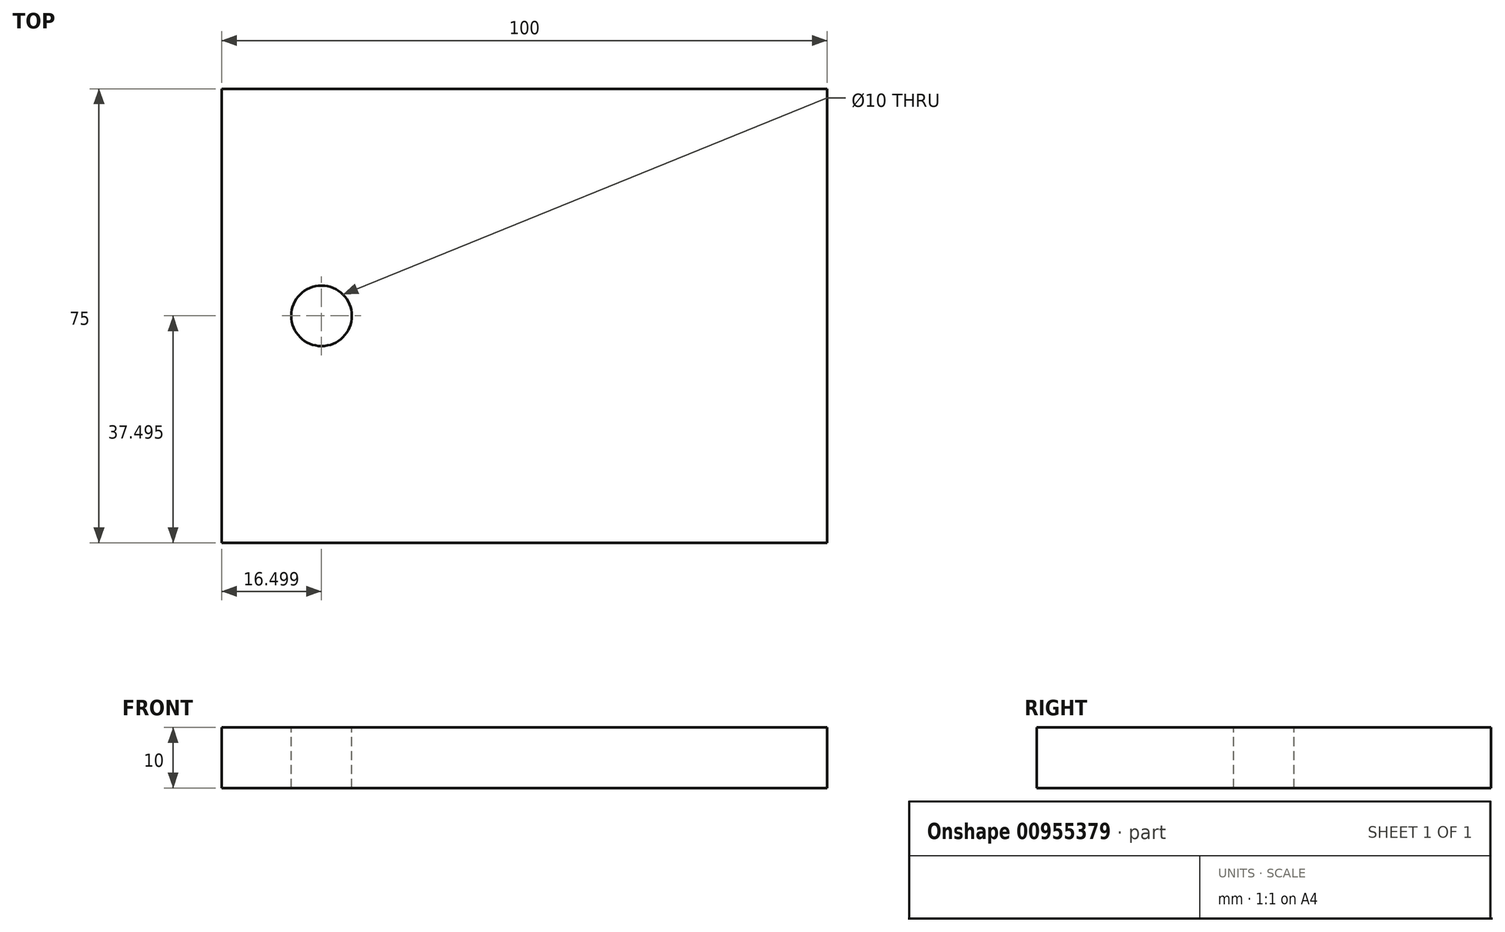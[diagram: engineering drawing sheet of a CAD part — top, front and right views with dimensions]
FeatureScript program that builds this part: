
annotation { "Feature Type Name" : "Feature", "Feature Type Description" : "" }
export const myFeature = defineFeature(function(context is Context, id is Id, definition is map)
    precondition{}
    {
        {
            var Q0;
            Q0=qCreatedBy(makeId("Top.planeOp"),FACE);
            var sketch = newSketch(context, id + "F0", { "sketchPlane" : qUnion([Q0])});
            skLineSegment(sketch, "E0.bottom", {"start": v(51.9, 49.62) * mm, "end": v(-48.1, 49.62) * mm});
            skLineSegment(sketch, "E0.top", {"start": v(51.9, -25.38) * mm, "end": v(-48.1, -25.38) * mm});
            skLineSegment(sketch, "E0.left", {"start": v(51.9, 49.62) * mm, "end": v(51.9, -25.38) * mm});
            skLineSegment(sketch, "E0.right", {"start": v(-48.1, 49.62) * mm, "end": v(-48.1, -25.38) * mm});
            skSolve(sketch);
        }
        {
            var Q0;
            Q0=makeQuery(id+"F0.imprint","IMPRINT",FACE,{"disambiguationData":[TD([[makeQuery(id+"F0.imprint","IMPRINT",EDGE,{"derivedFrom":sQuery(id+"F0.wireOp",EDGE,"E0.bottom")}),1.0]])]});
            extrude(context, id + "F1", {"entities" : qUnion([Q0]), "depth" : 10 * mm, "offsetDistance" : 25 * mm});
        }
        {
            var Q0;
            Q0=makeQuery(id+"F1.opExtrude","CAP_FACE",FACE,{"disambiguationData":[OSD([sQuery(id+"F0.wireOp",EDGE,"E0.bottom"),sQuery(id+"F0.wireOp",EDGE,"E0.top"),sQuery(id+"F0.wireOp",EDGE,"E0.left"),sQuery(id+"F0.wireOp",EDGE,"E0.right")])],"isStart":false});
            var sketch = newSketch(context, id + "F2", { "sketchPlane" : qUnion([Q0])});
            skCircle(sketch, "E1", {"center": v(-31.6, 12.12) * mm, "radius": 5 * mm});
            skPoint(sketch, "E1.centerSnap0", {"position": v(-48.1, 12.12) * mm});
            skSolve(sketch);
        }
        {
            var Q0;
            Q0=makeQuery(id+"F2.imprint","IMPRINT",FACE,{"disambiguationData":[TD([[makeQuery(id+"F2.imprint","IMPRINT",EDGE,{"derivedFrom":sQuery(id+"F2.wireOp",EDGE,"E1")}),1.0]])]});
            extrude(context, id + "F3", {"entities" : qUnion([Q0]), "operationType" : NewBodyOperationType.REMOVE, "oppositeDirection" : true, "depth" : 20 * mm, "offsetDistance" : 25 * mm});
        }
    });
